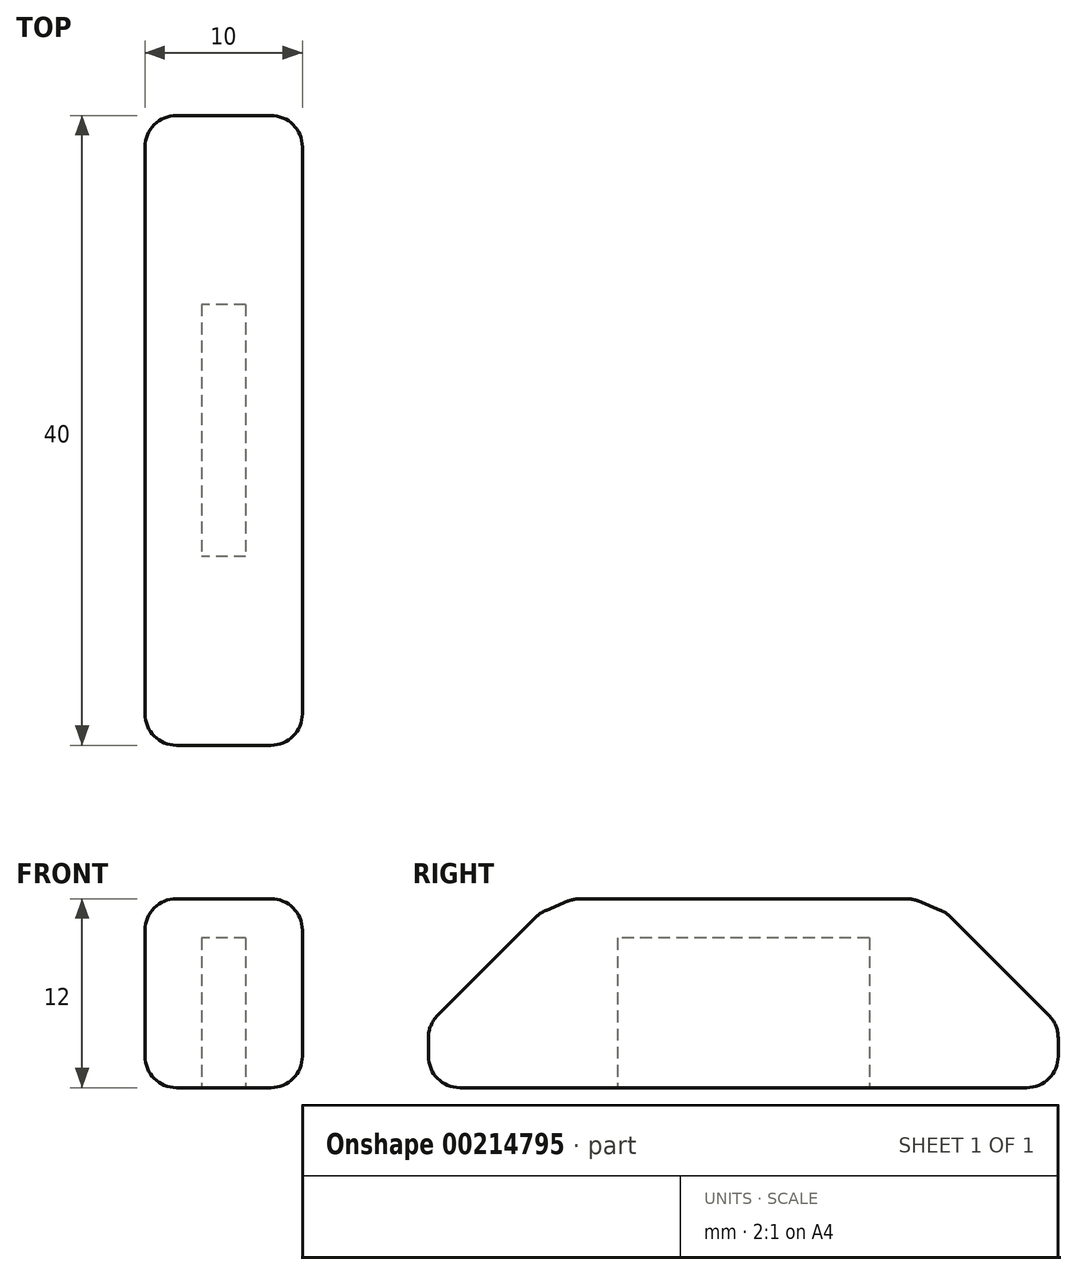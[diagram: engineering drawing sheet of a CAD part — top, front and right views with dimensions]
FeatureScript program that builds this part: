
annotation { "Feature Type Name" : "Feature", "Feature Type Description" : "" }
export const myFeature = defineFeature(function(context is Context, id is Id, definition is map)
    precondition{}
    {
        {
            var Q0;
            Q0=qCreatedBy(makeId("Front.planeOp"),FACE);
            var sketch = newSketch(context, id + "F0", { "sketchPlane" : qUnion([Q0])});
            skLineSegment(sketch, "E0.bottom", {"start": v(5, 6) * mm, "end": v(-5, 6) * mm});
            skLineSegment(sketch, "E0.top", {"start": v(5, -6) * mm, "end": v(-5, -6) * mm});
            skLineSegment(sketch, "E0.left", {"start": v(5, 6) * mm, "end": v(5, -6) * mm});
            skLineSegment(sketch, "E0.right", {"start": v(-5, 6) * mm, "end": v(-5, -6) * mm});
            skPoint(sketch, "E0.middle", {"position": v(0, 0) * mm});
            skSolve(sketch);
        }
        {
            var Q0;
            Q0 = qSketchRegion(id + "F0", true);
            extrude(context, id + "F1", {"entities" : qUnion([Q0]), "endBound" : BoundingType.SYMMETRIC, "depth" : 40 * mm});
        }
        {
            var Q0;
            Q0=makeQuery(id+"F1.opExtrude","SWEPT_FACE",FACE,{"disambiguationData":[OSD([sQuery(id+"F0.wireOp",EDGE,"E0.top")])]});
            var sketch = newSketch(context, id + "F2", { "sketchPlane" : qUnion([Q0])});
            skLineSegment(sketch, "E1.bottom", {"start": v(1.4, -8) * mm, "end": v(-1.4, -8) * mm});
            skLineSegment(sketch, "E1.top", {"start": v(1.4, 8) * mm, "end": v(-1.4, 8) * mm});
            skLineSegment(sketch, "E1.left", {"start": v(1.4, -8) * mm, "end": v(1.4, 8) * mm});
            skLineSegment(sketch, "E1.right", {"start": v(-1.4, -8) * mm, "end": v(-1.4, 8) * mm});
            skPoint(sketch, "E1.middle", {"position": v(0, 0) * mm});
            skSolve(sketch);
        }
        {
            var Q0;
            Q0 = qSketchRegion(id + "F2", true);
            extrude(context, id + "F3", {"entities" : qUnion([Q0]), "operationType" : NewBodyOperationType.REMOVE, "oppositeDirection" : true, "depth" : 9.5 * mm});
        }
        {
            var Q0;
            Q0=makeQuery(id+"F1.opExtrude","CAP_EDGE",EDGE,{"disambiguationData":[OSD([sQuery(id+"F0.wireOp",EDGE,"E0.bottom")])],"isStart":false});
            var Q1;
            Q1=makeQuery(id+"F1.opExtrude","CAP_EDGE",EDGE,{"disambiguationData":[OSD([sQuery(id+"F0.wireOp",EDGE,"E0.bottom")])],"isStart":true});
            chamfer(context, id + "F4", {"entities" : qUnion([Q0, Q1]), "width" : 8 * mm, "tangentPropagation" : true});
        }
        {
            var Q0;
            {var subQ0=sQuery(id+"F0.wireOp",EDGE,"E0.bottom");Q0=makeQuery(id+"F4.opChamfer","BLEND_EDGE",EDGE,{"blendedFrom":[makeQuery(id+"F1.opExtrude","CAP_EDGE",EDGE,{"disambiguationData":[OSD([subQ0])],"isStart":false}),makeQuery(id+"F1.opExtrude","SWEPT_FACE",FACE,{"disambiguationData":[OSD([subQ0])]})],"blendedInto":[makeQuery(id+"F1.opExtrude","SWEPT_FACE",FACE,{"disambiguationData":[OSD([subQ0])]})]});}
            var Q1;
            {var subQ0=sQuery(id+"F0.wireOp",EDGE,"E0.bottom");Q1=makeQuery(id+"F4.opChamfer","BLEND_EDGE",EDGE,{"blendedFrom":[makeQuery(id+"F1.opExtrude","CAP_EDGE",EDGE,{"disambiguationData":[OSD([subQ0])],"isStart":true}),makeQuery(id+"F1.opExtrude","SWEPT_FACE",FACE,{"disambiguationData":[OSD([subQ0])]})],"blendedInto":[makeQuery(id+"F1.opExtrude","SWEPT_FACE",FACE,{"disambiguationData":[OSD([subQ0])]})]});}
            chamfer(context, id + "F5", {"entities" : qUnion([Q0, Q1]), "width" : 3 * mm, "tangentPropagation" : true});
        }
        {
            var Q0;
            Q0=makeQuery(id+"F1.opExtrude","SWEPT_FACE",FACE,{"disambiguationData":[OSD([sQuery(id+"F0.wireOp",EDGE,"E0.left")])]});
            var Q1;
            Q1=makeQuery(id+"F1.opExtrude","SWEPT_FACE",FACE,{"disambiguationData":[OSD([sQuery(id+"F0.wireOp",EDGE,"E0.right")])]});
            var Q2;
            Q2=makeQuery(id+"F1.opExtrude","CAP_EDGE",EDGE,{"disambiguationData":[OSD([sQuery(id+"F0.wireOp",EDGE,"E0.top")])],"isStart":false});
            var Q3;
            Q3=makeQuery(id+"F1.opExtrude","CAP_EDGE",EDGE,{"disambiguationData":[OSD([sQuery(id+"F0.wireOp",EDGE,"E0.top")])],"isStart":true});
            var Q4;
            {var subQ0=sQuery(id+"F0.wireOp",EDGE,"E0.bottom");Q4=makeQuery(id+"F4.opChamfer","BLEND_EDGE",EDGE,{"blendedFrom":[makeQuery(id+"F1.opExtrude","CAP_EDGE",EDGE,{"disambiguationData":[OSD([subQ0])],"isStart":true}),makeQuery(id+"F1.opExtrude","CAP_FACE",FACE,{"disambiguationData":[OSD([subQ0,sQuery(id+"F0.wireOp",EDGE,"E0.top"),sQuery(id+"F0.wireOp",EDGE,"E0.left"),sQuery(id+"F0.wireOp",EDGE,"E0.right")])],"isStart":true})],"blendedInto":[makeQuery(id+"F1.opExtrude","CAP_FACE",FACE,{"disambiguationData":[OSD([subQ0,sQuery(id+"F0.wireOp",EDGE,"E0.top"),sQuery(id+"F0.wireOp",EDGE,"E0.left"),sQuery(id+"F0.wireOp",EDGE,"E0.right")])],"isStart":true})]});}
            var Q5;
            {var subQ0=sQuery(id+"F0.wireOp",EDGE,"E0.bottom");var subQ1=makeQuery(id+"F1.opExtrude","CAP_EDGE",EDGE,{"disambiguationData":[OSD([subQ0])],"isStart":true});Q5=makeQuery(id+"F5.opChamfer","BLEND_EDGE",EDGE,{"blendedFrom":[makeQuery(id+"F4.opChamfer","BLEND_EDGE",EDGE,{"blendedFrom":[subQ1,makeQuery(id+"F1.opExtrude","SWEPT_FACE",FACE,{"disambiguationData":[OSD([subQ0])]})],"blendedInto":[makeQuery(id+"F1.opExtrude","SWEPT_FACE",FACE,{"disambiguationData":[OSD([subQ0])]})]}),makeQuery(id+"F4.opChamfer","BLEND_FACE",FACE,{"disambiguationData":[OSD([subQ0]),TDD([subQ1])]})],"blendedInto":[makeQuery(id+"F4.opChamfer","BLEND_FACE",FACE,{"disambiguationData":[OSD([subQ0]),TDD([subQ1])]})]});}
            var Q6;
            {var subQ0=sQuery(id+"F0.wireOp",EDGE,"E0.bottom");var subQ1=makeQuery(id+"F1.opExtrude","SWEPT_FACE",FACE,{"disambiguationData":[OSD([subQ0])]});Q6=makeQuery(id+"F5.opChamfer","BLEND_EDGE",EDGE,{"blendedFrom":[makeQuery(id+"F4.opChamfer","BLEND_EDGE",EDGE,{"blendedFrom":[makeQuery(id+"F1.opExtrude","CAP_EDGE",EDGE,{"disambiguationData":[OSD([subQ0])],"isStart":true}),subQ1],"blendedInto":[subQ1]}),subQ1],"blendedInto":[subQ1]});}
            var Q7;
            {var subQ0=sQuery(id+"F0.wireOp",EDGE,"E0.bottom");var subQ1=makeQuery(id+"F1.opExtrude","SWEPT_FACE",FACE,{"disambiguationData":[OSD([subQ0])]});Q7=makeQuery(id+"F5.opChamfer","BLEND_EDGE",EDGE,{"blendedFrom":[makeQuery(id+"F4.opChamfer","BLEND_EDGE",EDGE,{"blendedFrom":[makeQuery(id+"F1.opExtrude","CAP_EDGE",EDGE,{"disambiguationData":[OSD([subQ0])],"isStart":false}),subQ1],"blendedInto":[subQ1]}),subQ1],"blendedInto":[subQ1]});}
            var Q8;
            {var subQ0=sQuery(id+"F0.wireOp",EDGE,"E0.bottom");var subQ1=makeQuery(id+"F1.opExtrude","CAP_EDGE",EDGE,{"disambiguationData":[OSD([subQ0])],"isStart":false});Q8=makeQuery(id+"F5.opChamfer","BLEND_EDGE",EDGE,{"blendedFrom":[makeQuery(id+"F4.opChamfer","BLEND_EDGE",EDGE,{"blendedFrom":[subQ1,makeQuery(id+"F1.opExtrude","SWEPT_FACE",FACE,{"disambiguationData":[OSD([subQ0])]})],"blendedInto":[makeQuery(id+"F1.opExtrude","SWEPT_FACE",FACE,{"disambiguationData":[OSD([subQ0])]})]}),makeQuery(id+"F4.opChamfer","BLEND_FACE",FACE,{"disambiguationData":[OSD([subQ0]),TDD([subQ1])]})],"blendedInto":[makeQuery(id+"F4.opChamfer","BLEND_FACE",FACE,{"disambiguationData":[OSD([subQ0]),TDD([subQ1])]})]});}
            var Q9;
            {var subQ0=sQuery(id+"F0.wireOp",EDGE,"E0.bottom");Q9=makeQuery(id+"F4.opChamfer","BLEND_EDGE",EDGE,{"blendedFrom":[makeQuery(id+"F1.opExtrude","CAP_EDGE",EDGE,{"disambiguationData":[OSD([subQ0])],"isStart":false}),makeQuery(id+"F1.opExtrude","CAP_FACE",FACE,{"disambiguationData":[OSD([subQ0,sQuery(id+"F0.wireOp",EDGE,"E0.top"),sQuery(id+"F0.wireOp",EDGE,"E0.left"),sQuery(id+"F0.wireOp",EDGE,"E0.right")])],"isStart":false})],"blendedInto":[makeQuery(id+"F1.opExtrude","CAP_FACE",FACE,{"disambiguationData":[OSD([subQ0,sQuery(id+"F0.wireOp",EDGE,"E0.top"),sQuery(id+"F0.wireOp",EDGE,"E0.left"),sQuery(id+"F0.wireOp",EDGE,"E0.right")])],"isStart":false})]});}
            fillet(context, id + "F6", {"entities" : qUnion([Q0, Q1, Q2, Q3, Q4, Q5, Q6, Q7, Q8, Q9]), "radius" : 2 * mm, "tangentPropagation" : true, "allowEdgeOverflow" : false});
        }
    });
